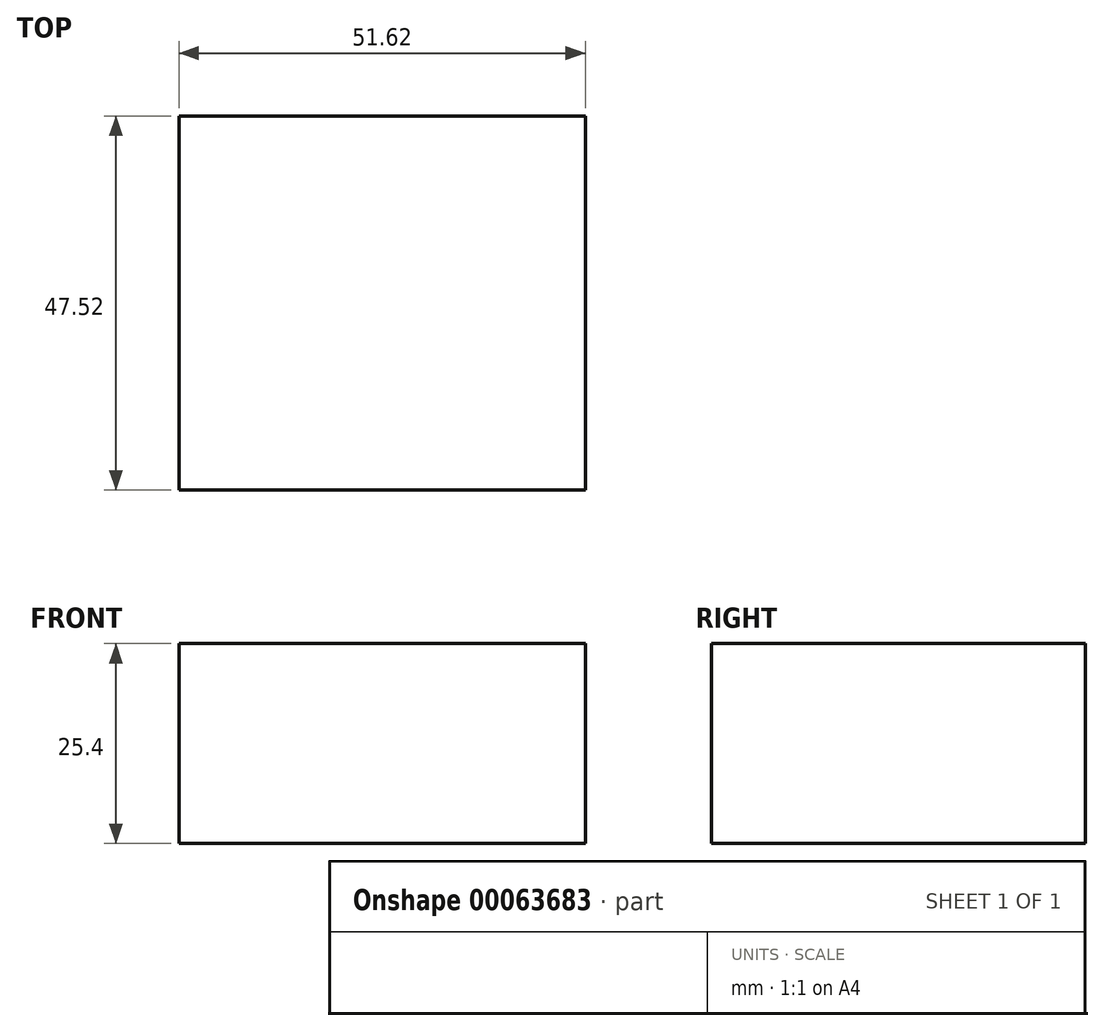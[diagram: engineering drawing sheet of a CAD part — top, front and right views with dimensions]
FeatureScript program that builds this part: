
annotation { "Feature Type Name" : "Feature", "Feature Type Description" : "" }
export const myFeature = defineFeature(function(context is Context, id is Id, definition is map)
    precondition{}
    {
        {
            var Q0;
            Q0=qCreatedBy(makeId("Top.planeOp"),FACE);
            var sketch = newSketch(context, id + "F0", { "sketchPlane" : qUnion([Q0])});
            skLineSegment(sketch, "E0.bottom", {"start": v(0, 0) * mm, "end": v(51.62, 0) * mm});
            skLineSegment(sketch, "E0.top", {"start": v(0, 47.52) * mm, "end": v(51.62, 47.52) * mm});
            skLineSegment(sketch, "E0.left", {"start": v(0, 0) * mm, "end": v(0, 47.52) * mm});
            skLineSegment(sketch, "E0.right", {"start": v(51.62, 0) * mm, "end": v(51.62, 47.52) * mm});
            skSolve(sketch);
        }
        {
            var Q0;
            Q0 = qSketchRegion(id + "F0", true);
            extrude(context, id + "F1", {"entities" : qUnion([Q0]), "depth" : 25.4 * mm});
        }
    });
